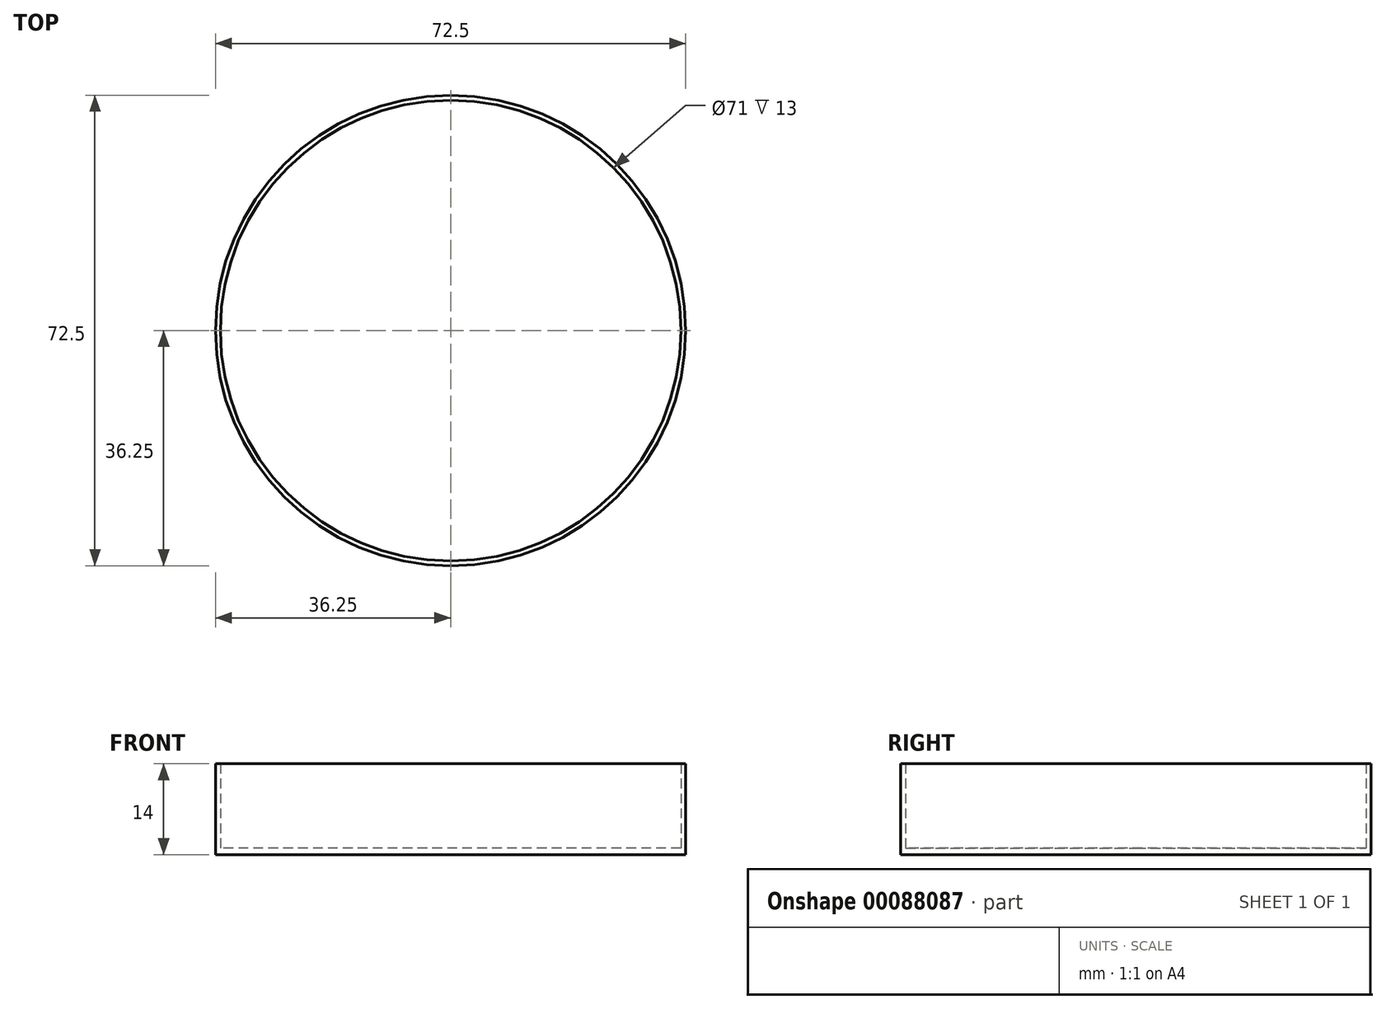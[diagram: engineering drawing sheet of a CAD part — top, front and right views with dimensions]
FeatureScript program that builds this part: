
annotation { "Feature Type Name" : "Feature", "Feature Type Description" : "" }
export const myFeature = defineFeature(function(context is Context, id is Id, definition is map)
    precondition{}
    {
        {
            var Q0;
            Q0=qCreatedBy(makeId("Top.planeOp"),FACE);
            var sketch = newSketch(context, id + "F0", { "sketchPlane" : qUnion([Q0])});
            skCircle(sketch, "E0", {"center": v(0, 0) * mm, "radius": 36.25 * mm});
            skSolve(sketch);
        }
        {
            var Q0;
            Q0 = qSketchRegion(id + "F0", true);
            extrude(context, id + "F1", {"entities" : qUnion([Q0]), "depth" : 1 * mm});
        }
        {
            var Q0;
            Q0=makeQuery(id+"F1.opExtrude","CAP_FACE",FACE,{"disambiguationData":[OSD([sQuery(id+"F0.wireOp",EDGE,"E0")])],"isStart":false});
            var sketch = newSketch(context, id + "F2", { "sketchPlane" : qUnion([Q0])});
            skCircle(sketch, "E1", {"center": v(0, 0) * mm, "radius": 35.5 * mm});
            skCircle(sketch, "E2", {"center": v(0, 0) * mm, "radius": 36.25 * mm});
            skSolve(sketch);
        }
        {
            var Q0;
            Q0 = qSketchRegion(id + "F2", true);
            extrude(context, id + "F3", {"entities" : qUnion([Q0]), "operationType" : NewBodyOperationType.ADD, "depth" : 13 * mm});
        }
    });
